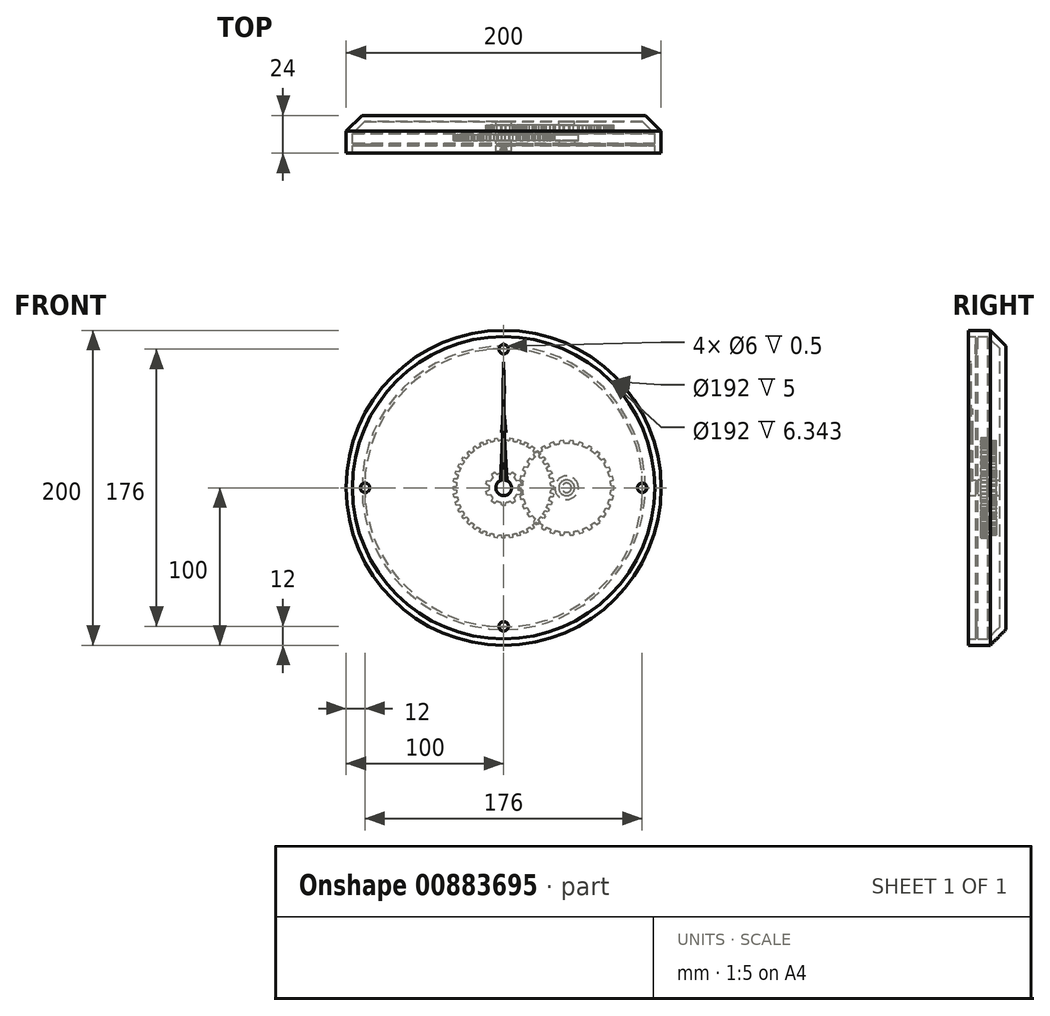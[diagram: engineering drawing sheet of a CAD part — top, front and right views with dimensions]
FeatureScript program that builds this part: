
annotation { "Feature Type Name" : "Feature", "Feature Type Description" : "" }
export const myFeature = defineFeature(function(context is Context, id is Id, definition is map)
    precondition{}
    {
        {
            var Q0;
            Q0=qCreatedBy(makeId("Front.planeOp"),FACE);
            var sketch = newSketch(context, id + "F0", { "sketchPlane" : qUnion([Q0])});
            skCircle(sketch, "E0", {"center": v(0, 0) * mm, "radius": 100 * mm});
            skSolve(sketch);
        }
        {
            var Q0;
            Q0 = qSketchRegion(id + "F0", true);
            extrude(context, id + "F1", {"entities" : qUnion([Q0]), "depth" : 24 * mm, "offsetDistance" : 25 * mm});
        }
        {
            var Q0;
            Q0=makeQuery(id+"F1.opExtrude","CAP_EDGE",EDGE,{"disambiguationData":[OSD([sQuery(id+"F0.wireOp",EDGE,"E0")])],"isStart":true});
            chamfer(context, id + "F2", {"entities" : qUnion([Q0]), "width" : 10 * mm, "tangentPropagation" : true});
        }
        {
            var Q0;
            Q0=makeQuery(id+"F1.opExtrude","CAP_FACE",FACE,{"disambiguationData":[OSD([sQuery(id+"F0.wireOp",EDGE,"E0")])],"isStart":false});
            shell(context, id + "F3", {"entities" : qUnion([Q0]), "thickness" : 4 * mm});
        }
        {
            var Q0;
            {var subQ0=sQuery(id+"F0.wireOp",EDGE,"E0");Q0=makeQuery(id+"F3.opShell","OFFSET_FACE",FACE,{"disambiguationData":[OSD([subQ0]),TDD([makeQuery(id+"F1.opExtrude","CAP_FACE",FACE,{"disambiguationData":[OSD([subQ0])],"isStart":true})])]});}
            var sketch = newSketch(context, id + "F4", { "sketchPlane" : qUnion([Q0])});
            skCircle(sketch, "E1", {"center": v(0, 0) * mm, "radius": 3 * mm});
            skCircle(sketch, "E2", {"center": v(0, 0) * mm, "radius": 5 * mm});
            skCircle(sketch, "E3", {"center": v(40, 0) * mm, "radius": 3 * mm});
            skCircle(sketch, "E4", {"center": v(40, 0) * mm, "radius": 5 * mm});
            skSolve(sketch);
        }
        {
            var Q0;
            Q0 = qSketchRegion(id + "F4", true);
            extrude(context, id + "F5", {"entities" : qUnion([Q0]), "operationType" : NewBodyOperationType.ADD, "depth" : 2 * mm, "offsetDistance" : 25 * mm});
        }
        {
            var Q0;
            {var subQ0=sQuery(id+"F0.wireOp",EDGE,"E0");Q0=makeQuery(id+"F5.boolean.opBoolean","SPLIT",FACE,{"disambiguationData":[TD([makeQuery(id+"F5.opExtrude","SWEPT_FACE",FACE,{"disambiguationData":[OSD([sQuery(id+"F4.wireOp",EDGE,"E1")])]})])],"derivedFrom":makeQuery(id+"F3.opShell","OFFSET_FACE",FACE,{"disambiguationData":[OSD([subQ0]),TDD([makeQuery(id+"F1.opExtrude","CAP_FACE",FACE,{"disambiguationData":[OSD([subQ0])],"isStart":true})])]})});}
            extrude(context, id + "F6", {"entities" : qUnion([Q0]), "depth" : 19 * mm, "offsetDistance" : 25 * mm});
        }
        {
            var Q0;
            {var subQ0=sQuery(id+"F0.wireOp",EDGE,"E0");Q0=makeQuery(id+"F5.boolean.opBoolean","SPLIT",FACE,{"disambiguationData":[TD([makeQuery(id+"F5.opExtrude","SWEPT_FACE",FACE,{"disambiguationData":[OSD([sQuery(id+"F4.wireOp",EDGE,"E3")])]})])],"derivedFrom":makeQuery(id+"F3.opShell","OFFSET_FACE",FACE,{"disambiguationData":[OSD([subQ0]),TDD([makeQuery(id+"F1.opExtrude","CAP_FACE",FACE,{"disambiguationData":[OSD([subQ0])],"isStart":true})])]})});}
            extrude(context, id + "F7", {"entities" : qUnion([Q0]), "depth" : 8 * mm, "offsetDistance" : 25 * mm});
        }
        {
            var Q0;
            Q0=makeQuery(id+"F5.opExtrude","CAP_FACE",FACE,{"disambiguationData":[OSD([sQuery(id+"F4.wireOp",EDGE,"E1"),sQuery(id+"F4.wireOp",EDGE,"E2")])],"isStart":false});
            var sketch = newSketch(context, id + "F8", { "sketchPlane" : qUnion([Q0])});
            skCircle(sketch, "E5", {"center": v(0, 0) * mm, "radius": 9.38 * mm});
            skLineSegment(sketch, "E6", {"start": v(0, 11.38) * mm, "end": v(1.18, 11.38) * mm});
            skLineSegment(sketch, "E7", {"start": v(1.18, 11.38) * mm, "end": v(1.55, 9.25) * mm});
            skLineSegment(sketch, "E8.MirrorCS", {"start": v(0, 11.38) * mm, "end": v(-1.18, 11.38) * mm});
            skLineSegment(sketch, "E9.MirrorCS", {"start": v(-1.18, 11.38) * mm, "end": v(-1.55, 9.25) * mm});
            skLineSegment(sketch, "E10.1.0", {"start": v(-5.73, 9.9) * mm, "end": v(-4.18, 8.4) * mm});
            skLineSegment(sketch, "E10.1.1", {"start": v(-6.69, 9.2) * mm, "end": v(-5.73, 9.9) * mm});
            skLineSegment(sketch, "E10.1.2", {"start": v(-6.69, 9.2) * mm, "end": v(-7.64, 8.51) * mm});
            skLineSegment(sketch, "E10.1.3", {"start": v(-7.64, 8.51) * mm, "end": v(-6.7, 6.57) * mm});
            skLineSegment(sketch, "E10.2.0", {"start": v(-10.45, 4.64) * mm, "end": v(-8.31, 4.33) * mm});
            skLineSegment(sketch, "E10.2.1", {"start": v(-10.82, 3.52) * mm, "end": v(-10.45, 4.64) * mm});
            skLineSegment(sketch, "E10.2.2", {"start": v(-10.82, 3.52) * mm, "end": v(-11.18, 2.4) * mm});
            skLineSegment(sketch, "E10.2.3", {"start": v(-11.18, 2.4) * mm, "end": v(-9.27, 1.38) * mm});
            skLineSegment(sketch, "E11.2.3.0", {"start": v(-11.18, -2.4) * mm, "end": v(-9.27, -1.38) * mm});
            skLineSegment(sketch, "E11.3.3.0", {"start": v(-10.82, -3.52) * mm, "end": v(-11.18, -2.4) * mm});
            skLineSegment(sketch, "E11.6.3.0", {"start": v(-10.82, -3.52) * mm, "end": v(-10.45, -4.64) * mm});
            skLineSegment(sketch, "E11.9.3.0", {"start": v(-10.45, -4.64) * mm, "end": v(-8.31, -4.33) * mm});
            skLineSegment(sketch, "E11.2.4.0", {"start": v(-7.64, -8.51) * mm, "end": v(-6.7, -6.57) * mm});
            skLineSegment(sketch, "E11.3.4.0", {"start": v(-6.69, -9.2) * mm, "end": v(-7.64, -8.51) * mm});
            skLineSegment(sketch, "E11.6.4.0", {"start": v(-6.69, -9.2) * mm, "end": v(-5.73, -9.9) * mm});
            skLineSegment(sketch, "E11.9.4.0", {"start": v(-5.73, -9.9) * mm, "end": v(-4.18, -8.4) * mm});
            skLineSegment(sketch, "E11.2.5.0", {"start": v(-1.18, -11.38) * mm, "end": v(-1.55, -9.25) * mm});
            skLineSegment(sketch, "E11.3.5.0", {"start": v(0, -11.38) * mm, "end": v(-1.18, -11.38) * mm});
            skLineSegment(sketch, "E11.6.5.0", {"start": v(0, -11.38) * mm, "end": v(1.18, -11.38) * mm});
            skLineSegment(sketch, "E11.9.5.0", {"start": v(1.18, -11.38) * mm, "end": v(1.55, -9.25) * mm});
            skLineSegment(sketch, "E11.2.6.0", {"start": v(5.73, -9.9) * mm, "end": v(4.18, -8.4) * mm});
            skLineSegment(sketch, "E11.3.6.0", {"start": v(6.69, -9.2) * mm, "end": v(5.73, -9.9) * mm});
            skLineSegment(sketch, "E11.6.6.0", {"start": v(6.69, -9.2) * mm, "end": v(7.64, -8.51) * mm});
            skLineSegment(sketch, "E11.9.6.0", {"start": v(7.64, -8.51) * mm, "end": v(6.7, -6.57) * mm});
            skLineSegment(sketch, "E11.2.7.0", {"start": v(10.45, -4.64) * mm, "end": v(8.31, -4.33) * mm});
            skLineSegment(sketch, "E11.3.7.0", {"start": v(10.82, -3.52) * mm, "end": v(10.45, -4.64) * mm});
            skLineSegment(sketch, "E11.6.7.0", {"start": v(10.82, -3.52) * mm, "end": v(11.18, -2.4) * mm});
            skLineSegment(sketch, "E11.9.7.0", {"start": v(11.18, -2.4) * mm, "end": v(9.27, -1.38) * mm});
            skLineSegment(sketch, "E11.2.8.0", {"start": v(11.18, 2.4) * mm, "end": v(9.27, 1.38) * mm});
            skLineSegment(sketch, "E11.3.8.0", {"start": v(10.82, 3.52) * mm, "end": v(11.18, 2.4) * mm});
            skLineSegment(sketch, "E11.6.8.0", {"start": v(10.82, 3.52) * mm, "end": v(10.45, 4.64) * mm});
            skLineSegment(sketch, "E11.9.8.0", {"start": v(10.45, 4.64) * mm, "end": v(8.31, 4.33) * mm});
            skLineSegment(sketch, "E11.2.9.0", {"start": v(7.64, 8.51) * mm, "end": v(6.7, 6.57) * mm});
            skLineSegment(sketch, "E11.3.9.0", {"start": v(6.69, 9.2) * mm, "end": v(7.64, 8.51) * mm});
            skLineSegment(sketch, "E11.6.9.0", {"start": v(6.69, 9.2) * mm, "end": v(5.73, 9.9) * mm});
            skLineSegment(sketch, "E11.9.9.0", {"start": v(5.73, 9.9) * mm, "end": v(4.18, 8.4) * mm});
            skSolve(sketch);
        }
        {
            var Q0;
            Q0 = qSketchRegion(id + "F8", true);
            extrude(context, id + "F9", {"entities" : qUnion([Q0]), "operationType" : NewBodyOperationType.ADD, "depth" : 4 * mm, "offsetDistance" : 25 * mm});
        }
        {
            var Q0;
            Q0=makeQuery(id+"F5.opExtrude","CAP_FACE",FACE,{"disambiguationData":[OSD([sQuery(id+"F4.wireOp",EDGE,"E3"),sQuery(id+"F4.wireOp",EDGE,"E4")])],"isStart":false});
            var sketch = newSketch(context, id + "F10", { "sketchPlane" : qUnion([Q0])});
            skCircle(sketch, "E12", {"center": v(40, 0) * mm, "radius": 28.12 * mm});
            skLineSegment(sketch, "E13", {"start": v(11.92, 1.54) * mm, "end": v(9.88, 1.18) * mm});
            skLineSegment(sketch, "E14", {"start": v(9.88, 1.18) * mm, "end": v(9.88, 0) * mm});
            skLineSegment(sketch, "E15.MirrorCS", {"start": v(9.88, -1.18) * mm, "end": v(9.88, 0) * mm});
            skLineSegment(sketch, "E16.MirrorCS", {"start": v(11.92, -1.54) * mm, "end": v(9.87, -1.18) * mm});
            skLineSegment(sketch, "E17.1.0", {"start": v(12.21, -4.33) * mm, "end": v(10.29, -5.11) * mm});
            skLineSegment(sketch, "E17.1.1", {"start": v(10.29, -5.11) * mm, "end": v(10.53, -6.26) * mm});
            skLineSegment(sketch, "E17.1.2", {"start": v(10.78, -7.42) * mm, "end": v(10.53, -6.26) * mm});
            skLineSegment(sketch, "E17.1.3", {"start": v(12.85, -7.34) * mm, "end": v(10.78, -7.42) * mm});
            skLineSegment(sketch, "E17.2.0", {"start": v(13.72, -10.02) * mm, "end": v(12, -11.18) * mm});
            skLineSegment(sketch, "E17.2.1", {"start": v(12, -11.18) * mm, "end": v(12.48, -12.25) * mm});
            skLineSegment(sketch, "E17.2.2", {"start": v(12.96, -13.33) * mm, "end": v(12.48, -12.25) * mm});
            skLineSegment(sketch, "E17.2.3", {"start": v(14.97, -12.83) * mm, "end": v(12.96, -13.33) * mm});
            skLineSegment(sketch, "E18.2.3.0", {"start": v(16.38, -15.26) * mm, "end": v(14.94, -16.75) * mm});
            skLineSegment(sketch, "E18.3.3.0", {"start": v(14.94, -16.75) * mm, "end": v(15.63, -17.7) * mm});
            skLineSegment(sketch, "E18.6.3.0", {"start": v(16.32, -18.66) * mm, "end": v(15.63, -17.7) * mm});
            skLineSegment(sketch, "E18.9.3.0", {"start": v(18.18, -17.75) * mm, "end": v(16.32, -18.66) * mm});
            skLineSegment(sketch, "E18.2.4.0", {"start": v(20.07, -19.84) * mm, "end": v(18.97, -21.6) * mm});
            skLineSegment(sketch, "E18.3.4.0", {"start": v(18.97, -21.6) * mm, "end": v(19.84, -22.39) * mm});
            skLineSegment(sketch, "E18.6.4.0", {"start": v(20.72, -23.18) * mm, "end": v(19.84, -22.39) * mm});
            skLineSegment(sketch, "E18.9.4.0", {"start": v(22.35, -21.9) * mm, "end": v(20.72, -23.18) * mm});
            skLineSegment(sketch, "E18.2.5.0", {"start": v(24.63, -23.55) * mm, "end": v(23.92, -25.5) * mm});
            skLineSegment(sketch, "E18.3.5.0", {"start": v(23.92, -25.5) * mm, "end": v(24.94, -26.09) * mm});
            skLineSegment(sketch, "E18.6.5.0", {"start": v(25.96, -26.68) * mm, "end": v(24.94, -26.09) * mm});
            skLineSegment(sketch, "E18.9.5.0", {"start": v(27.3, -25.09) * mm, "end": v(25.96, -26.68) * mm});
            skLineSegment(sketch, "E18.2.6.0", {"start": v(29.86, -26.23) * mm, "end": v(29.57, -28.29) * mm});
            skLineSegment(sketch, "E18.3.6.0", {"start": v(29.57, -28.29) * mm, "end": v(30.7, -28.65) * mm});
            skLineSegment(sketch, "E18.6.6.0", {"start": v(31.81, -29.01) * mm, "end": v(30.7, -28.65) * mm});
            skLineSegment(sketch, "E18.9.6.0", {"start": v(32.78, -27.18) * mm, "end": v(31.81, -29.01) * mm});
            skLineSegment(sketch, "E18.2.7.0", {"start": v(35.53, -27.77) * mm, "end": v(35.68, -29.84) * mm});
            skLineSegment(sketch, "E18.3.7.0", {"start": v(35.68, -29.84) * mm, "end": v(36.85, -29.96) * mm});
            skLineSegment(sketch, "E18.6.7.0", {"start": v(38.02, -30.08) * mm, "end": v(36.85, -29.96) * mm});
            skLineSegment(sketch, "E18.9.7.0", {"start": v(38.6, -28.09) * mm, "end": v(38.02, -30.08) * mm});
            skLineSegment(sketch, "E18.2.8.0", {"start": v(41.4, -28.09) * mm, "end": v(41.98, -30.08) * mm});
            skLineSegment(sketch, "E18.3.8.0", {"start": v(41.98, -30.08) * mm, "end": v(43.15, -29.96) * mm});
            skLineSegment(sketch, "E18.6.8.0", {"start": v(44.32, -29.84) * mm, "end": v(43.15, -29.96) * mm});
            skLineSegment(sketch, "E18.9.8.0", {"start": v(44.47, -27.77) * mm, "end": v(44.32, -29.84) * mm});
            skLineSegment(sketch, "E18.2.9.0", {"start": v(47.22, -27.18) * mm, "end": v(48.19, -29.01) * mm});
            skLineSegment(sketch, "E18.3.9.0", {"start": v(48.19, -29.01) * mm, "end": v(49.3, -28.65) * mm});
            skLineSegment(sketch, "E18.6.9.0", {"start": v(50.43, -28.29) * mm, "end": v(49.3, -28.65) * mm});
            skLineSegment(sketch, "E18.9.9.0", {"start": v(50.14, -26.23) * mm, "end": v(50.43, -28.29) * mm});
            skLineSegment(sketch, "E18.2.10.0", {"start": v(52.7, -25.09) * mm, "end": v(54.04, -26.68) * mm});
            skLineSegment(sketch, "E18.3.10.0", {"start": v(54.04, -26.68) * mm, "end": v(55.06, -26.09) * mm});
            skLineSegment(sketch, "E18.6.10.0", {"start": v(56.08, -25.5) * mm, "end": v(55.06, -26.09) * mm});
            skLineSegment(sketch, "E18.9.10.0", {"start": v(55.37, -23.55) * mm, "end": v(56.08, -25.5) * mm});
            skLineSegment(sketch, "E18.2.11.0", {"start": v(57.65, -21.9) * mm, "end": v(59.28, -23.18) * mm});
            skLineSegment(sketch, "E18.3.11.0", {"start": v(59.28, -23.18) * mm, "end": v(60.16, -22.39) * mm});
            skLineSegment(sketch, "E18.6.11.0", {"start": v(61.03, -21.6) * mm, "end": v(60.16, -22.39) * mm});
            skLineSegment(sketch, "E18.9.11.0", {"start": v(59.93, -19.84) * mm, "end": v(61.03, -21.6) * mm});
            skLineSegment(sketch, "E18.2.12.0", {"start": v(61.82, -17.75) * mm, "end": v(63.68, -18.66) * mm});
            skLineSegment(sketch, "E18.3.12.0", {"start": v(63.68, -18.66) * mm, "end": v(64.37, -17.7) * mm});
            skLineSegment(sketch, "E18.6.12.0", {"start": v(65.06, -16.75) * mm, "end": v(64.37, -17.7) * mm});
            skLineSegment(sketch, "E18.9.12.0", {"start": v(63.62, -15.26) * mm, "end": v(65.06, -16.75) * mm});
            skLineSegment(sketch, "E18.2.13.0", {"start": v(65.03, -12.83) * mm, "end": v(67.04, -13.33) * mm});
            skLineSegment(sketch, "E18.3.13.0", {"start": v(67.04, -13.33) * mm, "end": v(67.52, -12.25) * mm});
            skLineSegment(sketch, "E18.6.13.0", {"start": v(68, -11.18) * mm, "end": v(67.52, -12.25) * mm});
            skLineSegment(sketch, "E18.9.13.0", {"start": v(66.28, -10.02) * mm, "end": v(68, -11.18) * mm});
            skLineSegment(sketch, "E18.2.14.0", {"start": v(67.15, -7.34) * mm, "end": v(69.22, -7.42) * mm});
            skLineSegment(sketch, "E18.3.14.0", {"start": v(69.22, -7.42) * mm, "end": v(69.47, -6.26) * mm});
            skLineSegment(sketch, "E18.6.14.0", {"start": v(69.71, -5.11) * mm, "end": v(69.47, -6.26) * mm});
            skLineSegment(sketch, "E18.9.14.0", {"start": v(67.79, -4.33) * mm, "end": v(69.71, -5.11) * mm});
            skLineSegment(sketch, "E18.2.15.0", {"start": v(68.08, -1.54) * mm, "end": v(70.12, -1.18) * mm});
            skLineSegment(sketch, "E18.3.15.0", {"start": v(70.12, -1.18) * mm, "end": v(70.12, 0) * mm});
            skLineSegment(sketch, "E18.6.15.0", {"start": v(70.12, 1.18) * mm, "end": v(70.12, 0) * mm});
            skLineSegment(sketch, "E18.9.15.0", {"start": v(68.08, 1.54) * mm, "end": v(70.12, 1.18) * mm});
            skLineSegment(sketch, "E18.2.16.0", {"start": v(67.79, 4.33) * mm, "end": v(69.71, 5.11) * mm});
            skLineSegment(sketch, "E18.3.16.0", {"start": v(69.71, 5.11) * mm, "end": v(69.47, 6.26) * mm});
            skLineSegment(sketch, "E18.6.16.0", {"start": v(69.22, 7.42) * mm, "end": v(69.47, 6.26) * mm});
            skLineSegment(sketch, "E18.9.16.0", {"start": v(67.15, 7.34) * mm, "end": v(69.22, 7.42) * mm});
            skLineSegment(sketch, "E18.2.17.0", {"start": v(66.28, 10.02) * mm, "end": v(68, 11.18) * mm});
            skLineSegment(sketch, "E18.3.17.0", {"start": v(68, 11.18) * mm, "end": v(67.52, 12.25) * mm});
            skLineSegment(sketch, "E18.6.17.0", {"start": v(67.04, 13.33) * mm, "end": v(67.52, 12.25) * mm});
            skLineSegment(sketch, "E18.9.17.0", {"start": v(65.03, 12.83) * mm, "end": v(67.04, 13.33) * mm});
            skLineSegment(sketch, "E18.2.18.0", {"start": v(63.62, 15.26) * mm, "end": v(65.06, 16.75) * mm});
            skLineSegment(sketch, "E18.3.18.0", {"start": v(65.06, 16.75) * mm, "end": v(64.37, 17.7) * mm});
            skLineSegment(sketch, "E18.6.18.0", {"start": v(63.68, 18.66) * mm, "end": v(64.37, 17.7) * mm});
            skLineSegment(sketch, "E18.9.18.0", {"start": v(61.82, 17.75) * mm, "end": v(63.68, 18.66) * mm});
            skLineSegment(sketch, "E18.2.19.0", {"start": v(59.93, 19.84) * mm, "end": v(61.03, 21.6) * mm});
            skLineSegment(sketch, "E18.3.19.0", {"start": v(61.03, 21.6) * mm, "end": v(60.16, 22.39) * mm});
            skLineSegment(sketch, "E18.6.19.0", {"start": v(59.28, 23.18) * mm, "end": v(60.16, 22.39) * mm});
            skLineSegment(sketch, "E18.9.19.0", {"start": v(57.65, 21.9) * mm, "end": v(59.28, 23.18) * mm});
            skLineSegment(sketch, "E18.2.20.0", {"start": v(55.37, 23.55) * mm, "end": v(56.08, 25.5) * mm});
            skLineSegment(sketch, "E18.3.20.0", {"start": v(56.08, 25.5) * mm, "end": v(55.06, 26.09) * mm});
            skLineSegment(sketch, "E18.6.20.0", {"start": v(54.04, 26.68) * mm, "end": v(55.06, 26.09) * mm});
            skLineSegment(sketch, "E18.9.20.0", {"start": v(52.7, 25.09) * mm, "end": v(54.04, 26.68) * mm});
            skLineSegment(sketch, "E18.2.21.0", {"start": v(50.14, 26.23) * mm, "end": v(50.43, 28.29) * mm});
            skLineSegment(sketch, "E18.3.21.0", {"start": v(50.43, 28.29) * mm, "end": v(49.3, 28.65) * mm});
            skLineSegment(sketch, "E18.6.21.0", {"start": v(48.19, 29.01) * mm, "end": v(49.3, 28.65) * mm});
            skLineSegment(sketch, "E18.9.21.0", {"start": v(47.22, 27.18) * mm, "end": v(48.19, 29.01) * mm});
            skLineSegment(sketch, "E18.2.22.0", {"start": v(44.47, 27.77) * mm, "end": v(44.32, 29.84) * mm});
            skLineSegment(sketch, "E18.3.22.0", {"start": v(44.32, 29.84) * mm, "end": v(43.15, 29.96) * mm});
            skLineSegment(sketch, "E18.6.22.0", {"start": v(41.98, 30.08) * mm, "end": v(43.15, 29.96) * mm});
            skLineSegment(sketch, "E18.9.22.0", {"start": v(41.4, 28.09) * mm, "end": v(41.98, 30.08) * mm});
            skLineSegment(sketch, "E18.2.23.0", {"start": v(38.6, 28.09) * mm, "end": v(38.02, 30.08) * mm});
            skLineSegment(sketch, "E18.3.23.0", {"start": v(38.02, 30.08) * mm, "end": v(36.85, 29.96) * mm});
            skLineSegment(sketch, "E18.6.23.0", {"start": v(35.68, 29.84) * mm, "end": v(36.85, 29.96) * mm});
            skLineSegment(sketch, "E18.9.23.0", {"start": v(35.53, 27.77) * mm, "end": v(35.68, 29.84) * mm});
            skLineSegment(sketch, "E18.2.24.0", {"start": v(32.78, 27.18) * mm, "end": v(31.81, 29.01) * mm});
            skLineSegment(sketch, "E18.3.24.0", {"start": v(31.81, 29.01) * mm, "end": v(30.7, 28.65) * mm});
            skLineSegment(sketch, "E18.6.24.0", {"start": v(29.57, 28.29) * mm, "end": v(30.7, 28.65) * mm});
            skLineSegment(sketch, "E18.9.24.0", {"start": v(29.86, 26.23) * mm, "end": v(29.57, 28.29) * mm});
            skLineSegment(sketch, "E18.2.25.0", {"start": v(27.3, 25.09) * mm, "end": v(25.96, 26.68) * mm});
            skLineSegment(sketch, "E18.3.25.0", {"start": v(25.96, 26.68) * mm, "end": v(24.94, 26.09) * mm});
            skLineSegment(sketch, "E18.6.25.0", {"start": v(23.92, 25.5) * mm, "end": v(24.94, 26.09) * mm});
            skLineSegment(sketch, "E18.9.25.0", {"start": v(24.63, 23.55) * mm, "end": v(23.92, 25.5) * mm});
            skLineSegment(sketch, "E18.2.26.0", {"start": v(22.35, 21.9) * mm, "end": v(20.72, 23.18) * mm});
            skLineSegment(sketch, "E18.3.26.0", {"start": v(20.72, 23.18) * mm, "end": v(19.84, 22.39) * mm});
            skLineSegment(sketch, "E18.6.26.0", {"start": v(18.97, 21.6) * mm, "end": v(19.84, 22.39) * mm});
            skLineSegment(sketch, "E18.9.26.0", {"start": v(20.07, 19.84) * mm, "end": v(18.97, 21.6) * mm});
            skLineSegment(sketch, "E18.2.27.0", {"start": v(18.18, 17.75) * mm, "end": v(16.32, 18.66) * mm});
            skLineSegment(sketch, "E18.3.27.0", {"start": v(16.32, 18.66) * mm, "end": v(15.63, 17.7) * mm});
            skLineSegment(sketch, "E18.6.27.0", {"start": v(14.94, 16.75) * mm, "end": v(15.63, 17.7) * mm});
            skLineSegment(sketch, "E18.9.27.0", {"start": v(16.38, 15.26) * mm, "end": v(14.94, 16.75) * mm});
            skLineSegment(sketch, "E18.2.28.0", {"start": v(14.97, 12.83) * mm, "end": v(12.96, 13.33) * mm});
            skLineSegment(sketch, "E18.3.28.0", {"start": v(12.96, 13.33) * mm, "end": v(12.48, 12.25) * mm});
            skLineSegment(sketch, "E18.6.28.0", {"start": v(12, 11.18) * mm, "end": v(12.48, 12.25) * mm});
            skLineSegment(sketch, "E18.9.28.0", {"start": v(13.72, 10.02) * mm, "end": v(12, 11.18) * mm});
            skLineSegment(sketch, "E18.2.29.0", {"start": v(12.85, 7.34) * mm, "end": v(10.78, 7.42) * mm});
            skLineSegment(sketch, "E18.3.29.0", {"start": v(10.78, 7.42) * mm, "end": v(10.53, 6.26) * mm});
            skLineSegment(sketch, "E18.6.29.0", {"start": v(10.29, 5.11) * mm, "end": v(10.53, 6.26) * mm});
            skLineSegment(sketch, "E18.9.29.0", {"start": v(12.21, 4.33) * mm, "end": v(10.29, 5.11) * mm});
            skSolve(sketch);
        }
        {
            var Q0;
            Q0 = qSketchRegion(id + "F10", true);
            extrude(context, id + "F11", {"entities" : qUnion([Q0]), "operationType" : NewBodyOperationType.ADD, "depth" : 4 * mm, "offsetDistance" : 25 * mm});
        }
        {
            var Q0;
            Q0=makeQuery(id+"F9.opExtrude","CAP_FACE",FACE,{"disambiguationData":[OSD([sQuery(id+"F8.wireOp",EDGE,"E5")])],"isStart":false});
            var sketch = newSketch(context, id + "F12", { "sketchPlane" : qUnion([Q0])});
            skCircle(sketch, "E19.0", {"center": v(0, 0) * mm, "radius": 3 * mm});
            skCircle(sketch, "E20.0", {"center": v(0, 0) * mm, "radius": 5 * mm});
            skSolve(sketch);
        }
        {
            var Q0;
            Q0 = qSketchRegion(id + "F12", true);
            extrude(context, id + "F13", {"entities" : qUnion([Q0]), "depth" : 2 * mm, "offsetDistance" : 25 * mm});
        }
        {
            var Q0;
            Q0=makeQuery(id+"F13.opExtrude","CAP_FACE",FACE,{"disambiguationData":[OSD([sQuery(id+"F12.wireOp",EDGE,"E19.0"),sQuery(id+"F12.wireOp",EDGE,"E20.0")])],"isStart":false});
            var sketch = newSketch(context, id + "F14", { "sketchPlane" : qUnion([Q0])});
            skCircle(sketch, "E21.0", {"center": v(0, 0) * mm, "radius": 3 * mm});
            skCircle(sketch, "E22", {"center": v(0, 0) * mm, "radius": 30 * mm});
            skLineSegment(sketch, "E23", {"start": v(0, 32) * mm, "end": v(-0.94, 32) * mm});
            skLineSegment(sketch, "E24", {"start": v(-0.94, 32) * mm, "end": v(-1.3, 29.97) * mm});
            skLineSegment(sketch, "E25.MirrorCS", {"start": v(0, 32) * mm, "end": v(0.94, 32) * mm});
            skLineSegment(sketch, "E26.MirrorCS", {"start": v(0.94, 32) * mm, "end": v(1.3, 29.97) * mm});
            skLineSegment(sketch, "E27.1.0", {"start": v(-4.08, 31.75) * mm, "end": v(-3.4, 29.8) * mm});
            skLineSegment(sketch, "E27.1.1", {"start": v(-5, 31.6) * mm, "end": v(-4.08, 31.75) * mm});
            skLineSegment(sketch, "E27.1.2", {"start": v(-5, 31.6) * mm, "end": v(-5.94, 31.46) * mm});
            skLineSegment(sketch, "E27.1.3", {"start": v(-5.94, 31.46) * mm, "end": v(-5.97, 29.4) * mm});
            skLineSegment(sketch, "E27.2.0", {"start": v(-9, 30.73) * mm, "end": v(-8.03, 28.9) * mm});
            skLineSegment(sketch, "E27.2.1", {"start": v(-9.89, 30.43) * mm, "end": v(-9, 30.73) * mm});
            skLineSegment(sketch, "E27.2.2", {"start": v(-9.89, 30.43) * mm, "end": v(-10.78, 30.14) * mm});
            skLineSegment(sketch, "E27.2.3", {"start": v(-10.78, 30.14) * mm, "end": v(-10.5, 28.1) * mm});
            skLineSegment(sketch, "E28.2.3.0", {"start": v(-13.69, 28.94) * mm, "end": v(-12.45, 27.3) * mm});
            skLineSegment(sketch, "E28.3.3.0", {"start": v(-14.53, 28.51) * mm, "end": v(-13.69, 28.94) * mm});
            skLineSegment(sketch, "E28.6.3.0", {"start": v(-14.53, 28.51) * mm, "end": v(-15.37, 28.08) * mm});
            skLineSegment(sketch, "E28.9.3.0", {"start": v(-15.37, 28.08) * mm, "end": v(-14.77, 26.11) * mm});
            skLineSegment(sketch, "E28.2.4.0", {"start": v(-18.05, 26.44) * mm, "end": v(-16.57, 25.01) * mm});
            skLineSegment(sketch, "E28.3.4.0", {"start": v(-18.8, 25.89) * mm, "end": v(-18.05, 26.44) * mm});
            skLineSegment(sketch, "E28.6.4.0", {"start": v(-18.8, 25.89) * mm, "end": v(-19.57, 25.33) * mm});
            skLineSegment(sketch, "E28.9.4.0", {"start": v(-19.57, 25.33) * mm, "end": v(-18.67, 23.48) * mm});
            skLineSegment(sketch, "E28.2.5.0", {"start": v(-21.96, 23.3) * mm, "end": v(-20.27, 22.11) * mm});
            skLineSegment(sketch, "E28.3.5.0", {"start": v(-22.63, 22.63) * mm, "end": v(-21.96, 23.3) * mm});
            skLineSegment(sketch, "E28.6.5.0", {"start": v(-22.63, 22.63) * mm, "end": v(-23.3, 21.96) * mm});
            skLineSegment(sketch, "E28.9.5.0", {"start": v(-23.3, 21.96) * mm, "end": v(-22.11, 20.27) * mm});
            skLineSegment(sketch, "E28.2.6.0", {"start": v(-25.33, 19.57) * mm, "end": v(-23.48, 18.67) * mm});
            skLineSegment(sketch, "E28.3.6.0", {"start": v(-25.89, 18.8) * mm, "end": v(-25.33, 19.57) * mm});
            skLineSegment(sketch, "E28.6.6.0", {"start": v(-25.89, 18.8) * mm, "end": v(-26.44, 18.05) * mm});
            skLineSegment(sketch, "E28.9.6.0", {"start": v(-26.44, 18.05) * mm, "end": v(-25.01, 16.57) * mm});
            skLineSegment(sketch, "E28.2.7.0", {"start": v(-28.08, 15.37) * mm, "end": v(-26.11, 14.77) * mm});
            skLineSegment(sketch, "E28.3.7.0", {"start": v(-28.51, 14.53) * mm, "end": v(-28.08, 15.37) * mm});
            skLineSegment(sketch, "E28.6.7.0", {"start": v(-28.51, 14.53) * mm, "end": v(-28.94, 13.69) * mm});
            skLineSegment(sketch, "E28.9.7.0", {"start": v(-28.94, 13.69) * mm, "end": v(-27.3, 12.45) * mm});
            skLineSegment(sketch, "E28.2.8.0", {"start": v(-30.14, 10.78) * mm, "end": v(-28.1, 10.5) * mm});
            skLineSegment(sketch, "E28.3.8.0", {"start": v(-30.43, 9.89) * mm, "end": v(-30.14, 10.78) * mm});
            skLineSegment(sketch, "E28.6.8.0", {"start": v(-30.43, 9.89) * mm, "end": v(-30.73, 9) * mm});
            skLineSegment(sketch, "E28.9.8.0", {"start": v(-30.73, 9) * mm, "end": v(-28.9, 8.03) * mm});
            skLineSegment(sketch, "E28.2.9.0", {"start": v(-31.46, 5.94) * mm, "end": v(-29.4, 5.97) * mm});
            skLineSegment(sketch, "E28.3.9.0", {"start": v(-31.6, 5) * mm, "end": v(-31.46, 5.94) * mm});
            skLineSegment(sketch, "E28.6.9.0", {"start": v(-31.6, 5) * mm, "end": v(-31.75, 4.08) * mm});
            skLineSegment(sketch, "E28.9.9.0", {"start": v(-31.75, 4.08) * mm, "end": v(-29.8, 3.4) * mm});
            skLineSegment(sketch, "E28.2.10.0", {"start": v(-32, 0.94) * mm, "end": v(-29.97, 1.3) * mm});
            skLineSegment(sketch, "E28.3.10.0", {"start": v(-32, 0) * mm, "end": v(-32, 0.94) * mm});
            skLineSegment(sketch, "E28.6.10.0", {"start": v(-32, 0) * mm, "end": v(-32, -0.94) * mm});
            skLineSegment(sketch, "E28.9.10.0", {"start": v(-32, -0.94) * mm, "end": v(-29.97, -1.3) * mm});
            skLineSegment(sketch, "E28.2.11.0", {"start": v(-31.75, -4.08) * mm, "end": v(-29.8, -3.4) * mm});
            skLineSegment(sketch, "E28.3.11.0", {"start": v(-31.6, -5) * mm, "end": v(-31.75, -4.08) * mm});
            skLineSegment(sketch, "E28.6.11.0", {"start": v(-31.6, -5) * mm, "end": v(-31.46, -5.94) * mm});
            skLineSegment(sketch, "E28.9.11.0", {"start": v(-31.46, -5.94) * mm, "end": v(-29.4, -5.97) * mm});
            skLineSegment(sketch, "E28.2.12.0", {"start": v(-30.73, -9) * mm, "end": v(-28.9, -8.03) * mm});
            skLineSegment(sketch, "E28.3.12.0", {"start": v(-30.43, -9.89) * mm, "end": v(-30.73, -9) * mm});
            skLineSegment(sketch, "E28.6.12.0", {"start": v(-30.43, -9.89) * mm, "end": v(-30.14, -10.78) * mm});
            skLineSegment(sketch, "E28.9.12.0", {"start": v(-30.14, -10.78) * mm, "end": v(-28.1, -10.5) * mm});
            skLineSegment(sketch, "E28.2.13.0", {"start": v(-28.94, -13.69) * mm, "end": v(-27.3, -12.45) * mm});
            skLineSegment(sketch, "E28.3.13.0", {"start": v(-28.51, -14.53) * mm, "end": v(-28.94, -13.69) * mm});
            skLineSegment(sketch, "E28.6.13.0", {"start": v(-28.51, -14.53) * mm, "end": v(-28.08, -15.37) * mm});
            skLineSegment(sketch, "E28.9.13.0", {"start": v(-28.08, -15.37) * mm, "end": v(-26.11, -14.77) * mm});
            skLineSegment(sketch, "E28.2.14.0", {"start": v(-26.44, -18.05) * mm, "end": v(-25.01, -16.57) * mm});
            skLineSegment(sketch, "E28.3.14.0", {"start": v(-25.89, -18.8) * mm, "end": v(-26.44, -18.05) * mm});
            skLineSegment(sketch, "E28.6.14.0", {"start": v(-25.89, -18.8) * mm, "end": v(-25.33, -19.57) * mm});
            skLineSegment(sketch, "E28.9.14.0", {"start": v(-25.33, -19.57) * mm, "end": v(-23.48, -18.67) * mm});
            skLineSegment(sketch, "E28.2.15.0", {"start": v(-23.3, -21.96) * mm, "end": v(-22.11, -20.27) * mm});
            skLineSegment(sketch, "E28.3.15.0", {"start": v(-22.63, -22.63) * mm, "end": v(-23.3, -21.96) * mm});
            skLineSegment(sketch, "E28.6.15.0", {"start": v(-22.63, -22.63) * mm, "end": v(-21.96, -23.3) * mm});
            skLineSegment(sketch, "E28.9.15.0", {"start": v(-21.96, -23.3) * mm, "end": v(-20.27, -22.11) * mm});
            skLineSegment(sketch, "E28.2.16.0", {"start": v(-19.57, -25.33) * mm, "end": v(-18.67, -23.48) * mm});
            skLineSegment(sketch, "E28.3.16.0", {"start": v(-18.8, -25.89) * mm, "end": v(-19.57, -25.33) * mm});
            skLineSegment(sketch, "E28.6.16.0", {"start": v(-18.8, -25.89) * mm, "end": v(-18.05, -26.44) * mm});
            skLineSegment(sketch, "E28.9.16.0", {"start": v(-18.05, -26.44) * mm, "end": v(-16.57, -25.01) * mm});
            skLineSegment(sketch, "E28.2.17.0", {"start": v(-15.37, -28.08) * mm, "end": v(-14.77, -26.11) * mm});
            skLineSegment(sketch, "E28.3.17.0", {"start": v(-14.53, -28.51) * mm, "end": v(-15.37, -28.08) * mm});
            skLineSegment(sketch, "E28.6.17.0", {"start": v(-14.53, -28.51) * mm, "end": v(-13.69, -28.94) * mm});
            skLineSegment(sketch, "E28.9.17.0", {"start": v(-13.69, -28.94) * mm, "end": v(-12.45, -27.3) * mm});
            skLineSegment(sketch, "E28.2.18.0", {"start": v(-10.78, -30.14) * mm, "end": v(-10.5, -28.1) * mm});
            skLineSegment(sketch, "E28.3.18.0", {"start": v(-9.89, -30.43) * mm, "end": v(-10.78, -30.14) * mm});
            skLineSegment(sketch, "E28.6.18.0", {"start": v(-9.89, -30.43) * mm, "end": v(-9, -30.73) * mm});
            skLineSegment(sketch, "E28.9.18.0", {"start": v(-9, -30.73) * mm, "end": v(-8.03, -28.9) * mm});
            skLineSegment(sketch, "E28.2.19.0", {"start": v(-5.94, -31.46) * mm, "end": v(-5.97, -29.4) * mm});
            skLineSegment(sketch, "E28.3.19.0", {"start": v(-5, -31.6) * mm, "end": v(-5.94, -31.46) * mm});
            skLineSegment(sketch, "E28.6.19.0", {"start": v(-5, -31.6) * mm, "end": v(-4.08, -31.75) * mm});
            skLineSegment(sketch, "E28.9.19.0", {"start": v(-4.08, -31.75) * mm, "end": v(-3.4, -29.8) * mm});
            skLineSegment(sketch, "E28.2.20.0", {"start": v(-0.94, -32) * mm, "end": v(-1.3, -29.97) * mm});
            skLineSegment(sketch, "E28.3.20.0", {"start": v(0, -32) * mm, "end": v(-0.94, -32) * mm});
            skLineSegment(sketch, "E28.6.20.0", {"start": v(0, -32) * mm, "end": v(0.94, -32) * mm});
            skLineSegment(sketch, "E28.9.20.0", {"start": v(0.94, -32) * mm, "end": v(1.3, -29.97) * mm});
            skLineSegment(sketch, "E28.2.21.0", {"start": v(4.08, -31.75) * mm, "end": v(3.4, -29.8) * mm});
            skLineSegment(sketch, "E28.3.21.0", {"start": v(5, -31.6) * mm, "end": v(4.08, -31.75) * mm});
            skLineSegment(sketch, "E28.6.21.0", {"start": v(5, -31.6) * mm, "end": v(5.94, -31.46) * mm});
            skLineSegment(sketch, "E28.9.21.0", {"start": v(5.94, -31.46) * mm, "end": v(5.97, -29.4) * mm});
            skLineSegment(sketch, "E28.2.22.0", {"start": v(9, -30.73) * mm, "end": v(8.03, -28.9) * mm});
            skLineSegment(sketch, "E28.3.22.0", {"start": v(9.89, -30.43) * mm, "end": v(9, -30.73) * mm});
            skLineSegment(sketch, "E28.6.22.0", {"start": v(9.89, -30.43) * mm, "end": v(10.78, -30.14) * mm});
            skLineSegment(sketch, "E28.9.22.0", {"start": v(10.78, -30.14) * mm, "end": v(10.5, -28.1) * mm});
            skLineSegment(sketch, "E28.2.23.0", {"start": v(13.69, -28.94) * mm, "end": v(12.45, -27.3) * mm});
            skLineSegment(sketch, "E28.3.23.0", {"start": v(14.53, -28.51) * mm, "end": v(13.69, -28.94) * mm});
            skLineSegment(sketch, "E28.6.23.0", {"start": v(14.53, -28.51) * mm, "end": v(15.37, -28.08) * mm});
            skLineSegment(sketch, "E28.9.23.0", {"start": v(15.37, -28.08) * mm, "end": v(14.77, -26.11) * mm});
            skLineSegment(sketch, "E28.2.24.0", {"start": v(18.05, -26.44) * mm, "end": v(16.57, -25.01) * mm});
            skLineSegment(sketch, "E28.3.24.0", {"start": v(18.8, -25.89) * mm, "end": v(18.05, -26.44) * mm});
            skLineSegment(sketch, "E28.6.24.0", {"start": v(18.8, -25.89) * mm, "end": v(19.57, -25.33) * mm});
            skLineSegment(sketch, "E28.9.24.0", {"start": v(19.57, -25.33) * mm, "end": v(18.67, -23.48) * mm});
            skLineSegment(sketch, "E28.2.25.0", {"start": v(21.96, -23.3) * mm, "end": v(20.27, -22.11) * mm});
            skLineSegment(sketch, "E28.3.25.0", {"start": v(22.63, -22.63) * mm, "end": v(21.96, -23.3) * mm});
            skLineSegment(sketch, "E28.6.25.0", {"start": v(22.63, -22.63) * mm, "end": v(23.3, -21.96) * mm});
            skLineSegment(sketch, "E28.9.25.0", {"start": v(23.3, -21.96) * mm, "end": v(22.11, -20.27) * mm});
            skLineSegment(sketch, "E28.2.26.0", {"start": v(25.33, -19.57) * mm, "end": v(23.48, -18.67) * mm});
            skLineSegment(sketch, "E28.3.26.0", {"start": v(25.89, -18.8) * mm, "end": v(25.33, -19.57) * mm});
            skLineSegment(sketch, "E28.6.26.0", {"start": v(25.89, -18.8) * mm, "end": v(26.44, -18.05) * mm});
            skLineSegment(sketch, "E28.9.26.0", {"start": v(26.44, -18.05) * mm, "end": v(25.01, -16.57) * mm});
            skLineSegment(sketch, "E28.2.27.0", {"start": v(28.08, -15.37) * mm, "end": v(26.11, -14.77) * mm});
            skLineSegment(sketch, "E28.3.27.0", {"start": v(28.51, -14.53) * mm, "end": v(28.08, -15.37) * mm});
            skLineSegment(sketch, "E28.6.27.0", {"start": v(28.51, -14.53) * mm, "end": v(28.94, -13.69) * mm});
            skLineSegment(sketch, "E28.9.27.0", {"start": v(28.94, -13.69) * mm, "end": v(27.3, -12.45) * mm});
            skLineSegment(sketch, "E28.2.28.0", {"start": v(30.14, -10.78) * mm, "end": v(28.1, -10.5) * mm});
            skLineSegment(sketch, "E28.3.28.0", {"start": v(30.43, -9.89) * mm, "end": v(30.14, -10.78) * mm});
            skLineSegment(sketch, "E28.6.28.0", {"start": v(30.43, -9.89) * mm, "end": v(30.73, -9) * mm});
            skLineSegment(sketch, "E28.9.28.0", {"start": v(30.73, -9) * mm, "end": v(28.9, -8.03) * mm});
            skLineSegment(sketch, "E28.2.29.0", {"start": v(31.46, -5.94) * mm, "end": v(29.4, -5.97) * mm});
            skLineSegment(sketch, "E28.3.29.0", {"start": v(31.6, -5) * mm, "end": v(31.46, -5.94) * mm});
            skLineSegment(sketch, "E28.6.29.0", {"start": v(31.6, -5) * mm, "end": v(31.75, -4.08) * mm});
            skLineSegment(sketch, "E28.9.29.0", {"start": v(31.75, -4.08) * mm, "end": v(29.8, -3.4) * mm});
            skLineSegment(sketch, "E28.2.30.0", {"start": v(32, -0.94) * mm, "end": v(29.97, -1.3) * mm});
            skLineSegment(sketch, "E28.3.30.0", {"start": v(32, 0) * mm, "end": v(32, -0.94) * mm});
            skLineSegment(sketch, "E28.6.30.0", {"start": v(32, 0) * mm, "end": v(32, 0.94) * mm});
            skLineSegment(sketch, "E28.9.30.0", {"start": v(32, 0.94) * mm, "end": v(29.97, 1.3) * mm});
            skLineSegment(sketch, "E28.2.31.0", {"start": v(31.75, 4.08) * mm, "end": v(29.8, 3.4) * mm});
            skLineSegment(sketch, "E28.3.31.0", {"start": v(31.6, 5) * mm, "end": v(31.75, 4.08) * mm});
            skLineSegment(sketch, "E28.6.31.0", {"start": v(31.6, 5) * mm, "end": v(31.46, 5.94) * mm});
            skLineSegment(sketch, "E28.9.31.0", {"start": v(31.46, 5.94) * mm, "end": v(29.4, 5.97) * mm});
            skLineSegment(sketch, "E28.2.32.0", {"start": v(30.73, 9) * mm, "end": v(28.9, 8.03) * mm});
            skLineSegment(sketch, "E28.3.32.0", {"start": v(30.43, 9.89) * mm, "end": v(30.73, 9) * mm});
            skLineSegment(sketch, "E28.6.32.0", {"start": v(30.43, 9.89) * mm, "end": v(30.14, 10.78) * mm});
            skLineSegment(sketch, "E28.9.32.0", {"start": v(30.14, 10.78) * mm, "end": v(28.1, 10.5) * mm});
            skLineSegment(sketch, "E28.2.33.0", {"start": v(28.94, 13.69) * mm, "end": v(27.3, 12.45) * mm});
            skLineSegment(sketch, "E28.3.33.0", {"start": v(28.51, 14.53) * mm, "end": v(28.94, 13.69) * mm});
            skLineSegment(sketch, "E28.6.33.0", {"start": v(28.51, 14.53) * mm, "end": v(28.08, 15.37) * mm});
            skLineSegment(sketch, "E28.9.33.0", {"start": v(28.08, 15.37) * mm, "end": v(26.11, 14.77) * mm});
            skLineSegment(sketch, "E28.2.34.0", {"start": v(26.44, 18.05) * mm, "end": v(25.01, 16.57) * mm});
            skLineSegment(sketch, "E28.3.34.0", {"start": v(25.89, 18.8) * mm, "end": v(26.44, 18.05) * mm});
            skLineSegment(sketch, "E28.6.34.0", {"start": v(25.89, 18.8) * mm, "end": v(25.33, 19.57) * mm});
            skLineSegment(sketch, "E28.9.34.0", {"start": v(25.33, 19.57) * mm, "end": v(23.48, 18.67) * mm});
            skLineSegment(sketch, "E28.2.35.0", {"start": v(23.3, 21.96) * mm, "end": v(22.11, 20.27) * mm});
            skLineSegment(sketch, "E28.3.35.0", {"start": v(22.63, 22.63) * mm, "end": v(23.3, 21.96) * mm});
            skLineSegment(sketch, "E28.6.35.0", {"start": v(22.63, 22.63) * mm, "end": v(21.96, 23.3) * mm});
            skLineSegment(sketch, "E28.9.35.0", {"start": v(21.96, 23.3) * mm, "end": v(20.27, 22.11) * mm});
            skLineSegment(sketch, "E28.2.36.0", {"start": v(19.57, 25.33) * mm, "end": v(18.67, 23.48) * mm});
            skLineSegment(sketch, "E28.3.36.0", {"start": v(18.8, 25.89) * mm, "end": v(19.57, 25.33) * mm});
            skLineSegment(sketch, "E28.6.36.0", {"start": v(18.8, 25.89) * mm, "end": v(18.05, 26.44) * mm});
            skLineSegment(sketch, "E28.9.36.0", {"start": v(18.05, 26.44) * mm, "end": v(16.57, 25.01) * mm});
            skLineSegment(sketch, "E28.2.37.0", {"start": v(15.37, 28.08) * mm, "end": v(14.77, 26.11) * mm});
            skLineSegment(sketch, "E28.3.37.0", {"start": v(14.53, 28.51) * mm, "end": v(15.37, 28.08) * mm});
            skLineSegment(sketch, "E28.6.37.0", {"start": v(14.53, 28.51) * mm, "end": v(13.69, 28.94) * mm});
            skLineSegment(sketch, "E28.9.37.0", {"start": v(13.69, 28.94) * mm, "end": v(12.45, 27.3) * mm});
            skLineSegment(sketch, "E28.2.38.0", {"start": v(10.78, 30.14) * mm, "end": v(10.5, 28.1) * mm});
            skLineSegment(sketch, "E28.3.38.0", {"start": v(9.89, 30.43) * mm, "end": v(10.78, 30.14) * mm});
            skLineSegment(sketch, "E28.6.38.0", {"start": v(9.89, 30.43) * mm, "end": v(9, 30.73) * mm});
            skLineSegment(sketch, "E28.9.38.0", {"start": v(9, 30.73) * mm, "end": v(8.03, 28.9) * mm});
            skLineSegment(sketch, "E28.2.39.0", {"start": v(5.94, 31.46) * mm, "end": v(5.97, 29.4) * mm});
            skLineSegment(sketch, "E28.3.39.0", {"start": v(5, 31.6) * mm, "end": v(5.94, 31.46) * mm});
            skLineSegment(sketch, "E28.6.39.0", {"start": v(5, 31.6) * mm, "end": v(4.08, 31.75) * mm});
            skLineSegment(sketch, "E28.9.39.0", {"start": v(4.08, 31.75) * mm, "end": v(3.4, 29.8) * mm});
            skSolve(sketch);
        }
        {
            var Q0;
            Q0 = qSketchRegion(id + "F14", true);
            extrude(context, id + "F15", {"entities" : qUnion([Q0]), "operationType" : NewBodyOperationType.ADD, "depth" : 4 * mm, "offsetDistance" : 25 * mm});
        }
        {
            var Q0;
            Q0=makeQuery(id+"F7.opExtrude","CAP_FACE",FACE,{"disambiguationData":[OSD([sQuery(id+"F0.wireOp",EDGE,"E0")])],"isStart":false});
            var sketch = newSketch(context, id + "F16", { "sketchPlane" : qUnion([Q0])});
            skCircle(sketch, "E29", {"center": v(40, 0) * mm, "radius": 7.5 * mm});
            skSolve(sketch);
        }
        {
            var Q0;
            Q0 = qSketchRegion(id + "F16", true);
            extrude(context, id + "F17", {"entities" : qUnion([Q0]), "operationType" : NewBodyOperationType.ADD, "depth" : 4 * mm, "offsetDistance" : 25 * mm});
        }
        {
            var Q0;
            Q0=makeQuery(id+"F17.opExtrude","CAP_FACE",FACE,{"disambiguationData":[OSD([sQuery(id+"F16.wireOp",EDGE,"E29")])],"isStart":false});
            var sketch = newSketch(context, id + "F18", { "sketchPlane" : qUnion([Q0])});
            skCircle(sketch, "E30.0", {"center": v(40, 0) * mm, "radius": 3 * mm});
            skSolve(sketch);
        }
        {
            var Q0;
            Q0 = qSketchRegion(id + "F18", true);
            extrude(context, id + "F19", {"entities" : qUnion([Q0]), "operationType" : NewBodyOperationType.ADD, "depth" : 2 * mm, "offsetDistance" : 25 * mm});
        }
        {
            var Q0;
            Q0=makeQuery(id+"F19.opExtrude","CAP_FACE",FACE,{"disambiguationData":[OSD([sQuery(id+"F18.wireOp",EDGE,"E30.0")])],"isStart":false});
            var sketch = newSketch(context, id + "F20", { "sketchPlane" : qUnion([Q0])});
            skCircle(sketch, "E31", {"center": v(0, 0) * mm, "radius": 98 * mm});
            skCircle(sketch, "E32.0", {"center": v(0, 0) * mm, "radius": 5 * mm});
            skSolve(sketch);
        }
        {
            var Q0;
            Q0 = qSketchRegion(id + "F20", true);
            extrude(context, id + "F21", {"entities" : qUnion([Q0]), "depth" : 1 * mm, "offsetDistance" : 25 * mm});
        }
        {
            var Q0;
            Q0=makeQuery(id+"F21.opExtrude","SWEPT_BODY",BODY,{"disambiguationData":[OSD([sQuery(id+"F20.wireOp",EDGE,"E31"),sQuery(id+"F20.wireOp",EDGE,"E32.0")])]});
            var Q1;
            Q1=makeQuery(id+"F1.opExtrude","SWEPT_BODY",BODY,{"disambiguationData":[OSD([sQuery(id+"F0.wireOp",EDGE,"E0")])]});
            booleanBodies(context, id + "F22", {"operationType" : BooleanOperationType.SUBTRACTION, "tools" : qUnion([Q0]), "targets" : qUnion([Q1]), "keepTools" : true});
        }
        {
            var Q0;
            Q0=makeQuery(id+"F21.opExtrude","CAP_FACE",FACE,{"disambiguationData":[OSD([sQuery(id+"F20.wireOp",EDGE,"E31"),sQuery(id+"F20.wireOp",EDGE,"E32.0")])],"isStart":true});
            var sketch = newSketch(context, id + "F23", { "sketchPlane" : qUnion([Q0])});
            skCircle(sketch, "E33.0", {"center": v(-40, 0) * mm, "radius": 3 * mm});
            skCircle(sketch, "E34", {"center": v(-40, 0) * mm, "radius": 5 * mm});
            skSolve(sketch);
        }
        {
            var Q0;
            Q0 = qSketchRegion(id + "F23", true);
            extrude(context, id + "F24", {"entities" : qUnion([Q0]), "operationType" : NewBodyOperationType.ADD, "endBound" : BoundingType.UP_TO_NEXT, "depth" : 25 * mm, "offsetDistance" : 25 * mm});
        }
        {
            var Q0;
            Q0=makeQuery(id+"F21.opExtrude","CAP_FACE",FACE,{"disambiguationData":[OSD([sQuery(id+"F20.wireOp",EDGE,"E31"),sQuery(id+"F20.wireOp",EDGE,"E32.0")])],"isStart":false});
            var sketch = newSketch(context, id + "F25", { "sketchPlane" : qUnion([Q0])});
            skCircle(sketch, "E35", {"center": v(0, 88) * mm, "radius": 3 * mm});
            skCircle(sketch, "E36.1.0", {"center": v(-88, 0) * mm, "radius": 3 * mm});
            skCircle(sketch, "E36.2.0", {"center": v(0, -88) * mm, "radius": 3 * mm});
            skPoint(sketch, "E36.center", {"position": v(0, 0) * mm});
            skCircle(sketch, "E37.1.3.0", {"center": v(88, 0) * mm, "radius": 3 * mm});
            skSolve(sketch);
        }
        {
            var Q0;
            Q0 = qSketchRegion(id + "F25", true);
            extrude(context, id + "F26", {"entities" : qUnion([Q0]), "operationType" : NewBodyOperationType.REMOVE, "oppositeDirection" : true, "depth" : 0.5 * mm, "offsetDistance" : 25 * mm});
        }
        {
            var Q0;
            Q0=makeQuery(id+"F26.boolean.opBoolean","COPY",FACE,{"derivedFrom":makeQuery(id+"F26.opExtrude","CAP_FACE",FACE,{"disambiguationData":[OSD([sQuery(id+"F25.wireOp",EDGE,"E35")])],"isStart":false})});
            extrude(context, id + "F27", {"entities" : qUnion([Q0]), "depth" : 1 * mm, "offsetDistance" : 25 * mm});
        }
        {
            var Q0;
            Q0=makeQuery(id+"F15.opExtrude","CAP_FACE",FACE,{"disambiguationData":[OSD([sQuery(id+"F14.wireOp",EDGE,"E21.0"),sQuery(id+"F14.wireOp",EDGE,"E22")])],"isStart":false});
            var sketch = newSketch(context, id + "F28", { "sketchPlane" : qUnion([Q0])});
            skCircle(sketch, "E38.0", {"center": v(0, 0) * mm, "radius": 3 * mm});
            skCircle(sketch, "E39.0", {"center": v(0, 0) * mm, "radius": 5 * mm});
            skSolve(sketch);
        }
        {
            var Q0;
            Q0 = qSketchRegion(id + "F28", true);
            extrude(context, id + "F29", {"entities" : qUnion([Q0]), "operationType" : NewBodyOperationType.ADD, "depth" : 5 * mm, "offsetDistance" : 25 * mm});
        }
        {
            var Q0;
            Q0=makeQuery(id+"F29.opExtrude","CAP_FACE",FACE,{"disambiguationData":[OSD([sQuery(id+"F28.wireOp",EDGE,"E38.0"),sQuery(id+"F28.wireOp",EDGE,"E39.0")])],"isStart":false});
            var sketch = newSketch(context, id + "F30", { "sketchPlane" : qUnion([Q0])});
            skCircle(sketch, "E40.0", {"center": v(0, 0) * mm, "radius": 3 * mm});
            skCircle(sketch, "E41.0", {"center": v(0, 0) * mm, "radius": 5 * mm});
            skLineSegment(sketch, "E42", {"start": v(-2, 4.58) * mm, "end": v(-0.5, 35.08) * mm});
            skLineSegment(sketch, "E43", {"start": v(-0.5, 35.08) * mm, "end": v(-1.5, 35.08) * mm});
            skLineSegment(sketch, "E44", {"start": v(-1.5, 35.08) * mm, "end": v(0, 50) * mm});
            skLineSegment(sketch, "E45.MirrorCS", {"start": v(2, 4.58) * mm, "end": v(0.5, 35.08) * mm});
            skLineSegment(sketch, "E46.MirrorCS", {"start": v(0.5, 35.08) * mm, "end": v(1.5, 35.08) * mm});
            skLineSegment(sketch, "E47.MirrorCS", {"start": v(1.5, 35.08) * mm, "end": v(0, 50) * mm});
            skSolve(sketch);
        }
        {
            var Q0;
            Q0 = qSketchRegion(id + "F30", true);
            extrude(context, id + "F31", {"entities" : qUnion([Q0]), "operationType" : NewBodyOperationType.ADD, "depth" : 1 * mm, "offsetDistance" : 25 * mm});
        }
        {
            var Q0;
            Q0=makeQuery(id+"F6.opExtrude","CAP_FACE",FACE,{"disambiguationData":[OSD([sQuery(id+"F0.wireOp",EDGE,"E0")])],"isStart":false});
            var sketch = newSketch(context, id + "F32", { "sketchPlane" : qUnion([Q0])});
            skCircle(sketch, "E48", {"center": v(0, 0) * mm, "radius": 5 * mm});
            skLineSegment(sketch, "E49", {"start": v(-1, 4.9) * mm, "end": v(-0.3, 60) * mm});
            skLineSegment(sketch, "E50", {"start": v(-0.3, 60) * mm, "end": v(-0.5, 60) * mm});
            skLineSegment(sketch, "E51", {"start": v(-0.5, 60) * mm, "end": v(0, 80) * mm});
            skLineSegment(sketch, "E52.MirrorCS", {"start": v(1, 4.9) * mm, "end": v(0.3, 60) * mm});
            skLineSegment(sketch, "E53.MirrorCS", {"start": v(0.3, 60) * mm, "end": v(0.5, 60) * mm});
            skLineSegment(sketch, "E54.MirrorCS", {"start": v(0.5, 60) * mm, "end": v(0, 80) * mm});
            skSolve(sketch);
        }
        {
            var Q0;
            Q0 = qSketchRegion(id + "F32", true);
            extrude(context, id + "F33", {"entities" : qUnion([Q0]), "operationType" : NewBodyOperationType.ADD, "oppositeDirection" : true, "depth" : 1 * mm, "offsetDistance" : 25 * mm});
        }
    });
